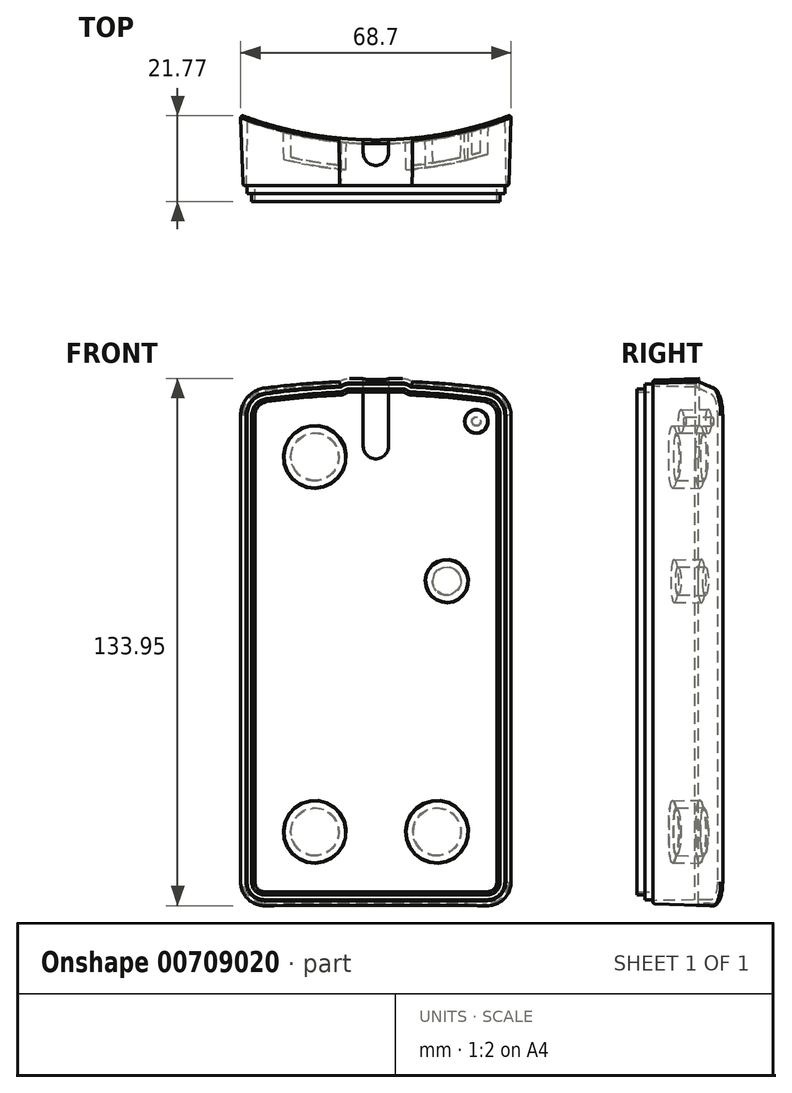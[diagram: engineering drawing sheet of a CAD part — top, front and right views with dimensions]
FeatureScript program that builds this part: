
annotation { "Feature Type Name" : "Feature", "Feature Type Description" : "" }
export const myFeature = defineFeature(function(context is Context, id is Id, definition is map)
    precondition{}
    {
        {
            var Q0;
            Q0=qCreatedBy(makeId("Front.planeOp"),FACE);
            var sketch = newSketch(context, id + "F0", { "sketchPlane" : qUnion([Q0])});
            skLineSegment(sketch, "E0.bottom", {"start": v(4.5, 0) * mm, "end": v(61, 0) * mm});
            skLineSegment(sketch, "E0.left", {"start": v(0, 4.5) * mm, "end": v(0, 123.05) * mm});
            skLineSegment(sketch, "E0.right", {"start": v(65.5, 4.5) * mm, "end": v(65.5, 123.05) * mm});
            skPoint(sketch, "E1.visualSharp", {"position": v(0, 0) * mm});
            skArc(sketch, "E1.filletArc", {"start": v(0, 4.5) * mm, "mid": v(1.32, 1.32) * mm, "end": v(4.5, 0) * mm});
            skPoint(sketch, "E2.visualSharp", {"position": v(65.5, 0) * mm});
            skArc(sketch, "E2.filletArc", {"start": v(61, 0) * mm, "mid": v(64.18, 1.32) * mm, "end": v(65.5, 4.5) * mm});
            skArc(sketch, "E3.filletArc", {"start": v(4.76, 128.5) * mm, "mid": v(1.36, 126.67) * mm, "end": v(0, 123.05) * mm});
            skPoint(sketch, "E4.visualSharp", {"position": v(65.5, 168.18) * mm});
            skArc(sketch, "E4.filletArc", {"start": v(65.5, 123.05) * mm, "mid": v(64.14, 126.67) * mm, "end": v(60.74, 128.5) * mm});
            skArc(sketch, "E5", {"start": v(60.74, 128.5) * mm, "mid": v(51.35, 129.57) * mm, "end": v(41.91, 130.2) * mm});
            skLineSegment(sketch, "E6", {"start": v(26, 131) * mm, "end": v(39.5, 131) * mm});
            skArc(sketch, "E7.trimOffspring", {"start": v(23.59, 130.2) * mm, "mid": v(14.15, 129.57) * mm, "end": v(4.76, 128.5) * mm});
            skLineSegment(sketch, "E8", {"start": v(32.75, 0) * mm, "end": v(32.75, 224.52) * mm, "construction": true});
            skArc(sketch, "E9", {"start": v(26, 131) * mm, "mid": v(25.02, 130.84) * mm, "end": v(24.13, 130.4) * mm});
            skPoint(sketch, "E10.visualSharp", {"position": v(23.91, 130.21) * mm});
            skArc(sketch, "E10.filletArc", {"start": v(23.59, 130.2) * mm, "mid": v(23.87, 130.26) * mm, "end": v(24.13, 130.4) * mm});
            skArc(sketch, "E11.MirrorCS", {"start": v(41.91, 130.2) * mm, "mid": v(41.63, 130.26) * mm, "end": v(41.37, 130.4) * mm});
            skArc(sketch, "E12.MirrorCS", {"start": v(39.5, 131) * mm, "mid": v(40.48, 130.84) * mm, "end": v(41.37, 130.4) * mm});
            skSolve(sketch);
        }
        {
            var Q0;
            Q0=qCreatedBy(makeId("Top.planeOp"),FACE);
            var sketch = newSketch(context, id + "F1", { "sketchPlane" : qUnion([Q0])});
            skArc(sketch, "E13", {"start": v(0, 0) * mm, "mid": v(32.75, -5.75) * mm, "end": v(65.5, 0) * mm});
            skLineSegment(sketch, "E14", {"start": v(0, 0) * mm, "end": v(65.5, 0) * mm});
            skLineSegment(sketch, "E15", {"start": v(0, 0) * mm, "end": v(94.5, 0) * mm, "construction": true});
            skLineSegment(sketch, "E16", {"start": v(94.5, 0) * mm, "end": v(32.75, 0) * mm, "construction": true});
            skLineSegment(sketch, "E17", {"start": v(32.75, 0) * mm, "end": v(32.75, -16.7) * mm, "construction": true});
            skSolve(sketch);
        }
        {
            var Q0;
            Q0=qSketchRegion(id+"F0",true);
            extrude(context, id + "F2", {"entities" : qUnion([Q0]), "depth" : 12.5 * mm, "offsetDistance" : 25 * mm});
        }
        {
            var Q0;
            Q0=qSketchRegion(id+"F1",true);
            extrude(context, id + "F3", {"entities" : qUnion([Q0]), "operationType" : NewBodyOperationType.REMOVE, "endBound" : BoundingType.THROUGH_ALL, "depth" : 25 * mm, "offsetDistance" : 25 * mm});
        }
        {
            var Q0;
            Q0=makeQuery(id+"F2.opExtrude","SWEPT_FACE",FACE,{"disambiguationData":[OSD([sQuery(id+"F0.wireOp",EDGE,"E0.bottom")])]});
            var sketch = newSketch(context, id + "F4", { "sketchPlane" : qUnion([Q0])});
            skLineSegment(sketch, "E18", {"start": v(0, 12.5) * mm, "end": v(0, 10.5) * mm});
            skLineSegment(sketch, "E19", {"start": v(0, 10.5) * mm, "end": v(1.1, 10.5) * mm});
            skLineSegment(sketch, "E20", {"start": v(1.1, 10.5) * mm, "end": v(1.1, 12.5) * mm});
            skLineSegment(sketch, "E21", {"start": v(1.1, 12.5) * mm, "end": v(0, 12.5) * mm});
            skSolve(sketch);
        }
        {
            var Q0;
            Q0=makeQuery(id+"F4.imprint","IMPRINT",FACE,{"disambiguationData":[TD([[makeQuery(id+"F4.imprint","IMPRINT",EDGE,{"derivedFrom":sQuery(id+"F4.wireOp",EDGE,"E18")}),1.0]])]});
            cPlane(context, id + "F5", {"entities" : qUnion([Q0]), "cplaneType" : CPlaneType.OFFSET, "offset" : 50 * mm, "oppositeDirection" : true, "width" : 150 * mm, "height" : 150 * mm});
        }
        {
            var Q0;
            Q0=makeQuery(id+"F2.opExtrude","CAP_FACE",FACE,{"disambiguationData":[OSD([sQuery(id+"F0.wireOp",EDGE,"E0.bottom"),sQuery(id+"F0.wireOp",EDGE,"E0.left"),sQuery(id+"F0.wireOp",EDGE,"E0.right"),sQuery(id+"F0.wireOp",EDGE,"E1.filletArc"),sQuery(id+"F0.wireOp",EDGE,"E2.filletArc"),sQuery(id+"F0.wireOp",EDGE,"E3.filletArc"),sQuery(id+"F0.wireOp",EDGE,"E4.filletArc"),sQuery(id+"F0.wireOp",EDGE,"E5"),sQuery(id+"F0.wireOp",EDGE,"E6"),sQuery(id+"F0.wireOp",EDGE,"4cuLOFSM-Cs9p-uLwk-Nxmp-eiNM5esqOte1"),sQuery(id+"F0.wireOp",EDGE,"qXNs2k06-4niP-ImqC-5Hru-JPzRlnRtqvzY"),sQuery(id+"F0.wireOp",EDGE,"592cab12-c6ad-4f12-8fa5-e9ea6a7a9ab5.filletArc"),sQuery(id+"F0.wireOp",EDGE,"E7.trimOffspring"),sQuery(id+"F0.wireOp",EDGE,"810a662d-7d86-4de4-b075-b749f1e53ed9.filletArc"),sQuery(id+"F0.wireOp",EDGE,"8d541c61-4af1-470d-ac14-312aa46fb37d.filletArc"),sQuery(id+"F0.wireOp",EDGE,"225b199f-dbc8-4900-9de2-33667acb90c7.filletArc")])],"isStart":false});
            shell(context, id + "F6", {"entities" : qUnion([Q0]), "thickness" : 2 * mm});
        }
        {
            var Q0;
            Q0=makeQuery(id+"F2.opExtrude","CAP_FACE",FACE,{"disambiguationData":[OSD([sQuery(id+"F0.wireOp",EDGE,"E0.bottom"),sQuery(id+"F0.wireOp",EDGE,"E0.left"),sQuery(id+"F0.wireOp",EDGE,"E0.right"),sQuery(id+"F0.wireOp",EDGE,"E1.filletArc"),sQuery(id+"F0.wireOp",EDGE,"E2.filletArc"),sQuery(id+"F0.wireOp",EDGE,"E3.filletArc"),sQuery(id+"F0.wireOp",EDGE,"E4.filletArc"),sQuery(id+"F0.wireOp",EDGE,"E5"),sQuery(id+"F0.wireOp",EDGE,"E6"),sQuery(id+"F0.wireOp",EDGE,"E7.trimOffspring"),sQuery(id+"F0.wireOp",EDGE,"E9"),sQuery(id+"F0.wireOp",EDGE,"E10.filletArc"),sQuery(id+"F0.wireOp",EDGE,"E11.MirrorCS"),sQuery(id+"F0.wireOp",EDGE,"E12.MirrorCS")])],"isStart":false});
            var sketch = newSketch(context, id + "F7", { "sketchPlane" : qUnion([Q0])});
            skLineSegment(sketch, "E22.0.0", {"start": v(39.5, 131) * mm, "end": v(26, 131) * mm});
            skArc(sketch, "E22.0.1", {"start": v(26, 131) * mm, "mid": v(25.02, 130.84) * mm, "end": v(24.13, 130.4) * mm});
            skArc(sketch, "E22.0.2", {"start": v(24.13, 130.4) * mm, "mid": v(23.87, 130.26) * mm, "end": v(23.59, 130.2) * mm});
            skArc(sketch, "E22.0.3", {"start": v(23.59, 130.2) * mm, "mid": v(14.15, 129.57) * mm, "end": v(4.76, 128.5) * mm});
            skArc(sketch, "E22.0.4", {"start": v(4.76, 128.5) * mm, "mid": v(1.36, 126.67) * mm, "end": v(0, 123.05) * mm});
            skLineSegment(sketch, "E22.0.5", {"start": v(0, 123.05) * mm, "end": v(0, 4.5) * mm});
            skArc(sketch, "E22.0.6", {"start": v(0, 4.5) * mm, "mid": v(1.32, 1.32) * mm, "end": v(4.5, 0) * mm});
            skLineSegment(sketch, "E22.0.7", {"start": v(4.5, 0) * mm, "end": v(61, 0) * mm});
            skArc(sketch, "E22.0.8", {"start": v(61, 0) * mm, "mid": v(64.18, 1.32) * mm, "end": v(65.5, 4.5) * mm});
            skLineSegment(sketch, "E22.0.9", {"start": v(65.5, 4.5) * mm, "end": v(65.5, 123.05) * mm});
            skArc(sketch, "E22.0.10", {"start": v(65.5, 123.05) * mm, "mid": v(64.14, 126.67) * mm, "end": v(60.74, 128.5) * mm});
            skArc(sketch, "E22.0.11", {"start": v(60.74, 128.5) * mm, "mid": v(51.35, 129.57) * mm, "end": v(41.91, 130.2) * mm});
            skArc(sketch, "E22.0.12", {"start": v(41.91, 130.2) * mm, "mid": v(41.63, 130.26) * mm, "end": v(41.37, 130.4) * mm});
            skArc(sketch, "E22.0.13", {"start": v(41.37, 130.4) * mm, "mid": v(40.48, 130.84) * mm, "end": v(39.5, 131) * mm});
            skArc(sketch, "E23.0", {"start": v(40.66, 129.42) * mm, "mid": v(40.1, 129.7) * mm, "end": v(39.5, 129.8) * mm});
            skArc(sketch, "E23.1", {"start": v(41.86, 129) * mm, "mid": v(41.23, 129.12) * mm, "end": v(40.66, 129.42) * mm});
            skArc(sketch, "E23.2", {"start": v(60.58, 127.31) * mm, "mid": v(51.24, 128.37) * mm, "end": v(41.86, 129) * mm});
            skArc(sketch, "E23.3", {"start": v(4.92, 127.31) * mm, "mid": v(2.26, 125.88) * mm, "end": v(1.2, 123.05) * mm});
            skArc(sketch, "E23.4", {"start": v(23.64, 129) * mm, "mid": v(14.26, 128.37) * mm, "end": v(4.92, 127.31) * mm});
            skArc(sketch, "E23.5", {"start": v(24.84, 129.42) * mm, "mid": v(24.27, 129.12) * mm, "end": v(23.64, 129) * mm});
            skArc(sketch, "E23.6", {"start": v(26, 129.8) * mm, "mid": v(25.4, 129.7) * mm, "end": v(24.84, 129.42) * mm});
            skLineSegment(sketch, "E23.7", {"start": v(1.2, 123.05) * mm, "end": v(1.2, 4.5) * mm});
            skArc(sketch, "E23.8", {"start": v(1.2, 4.5) * mm, "mid": v(2.17, 2.17) * mm, "end": v(4.5, 1.2) * mm});
            skLineSegment(sketch, "E23.9", {"start": v(4.5, 1.2) * mm, "end": v(61, 1.2) * mm});
            skLineSegment(sketch, "E23.10", {"start": v(39.5, 129.8) * mm, "end": v(26, 129.8) * mm});
            skArc(sketch, "E23.11", {"start": v(61, 1.2) * mm, "mid": v(63.33, 2.17) * mm, "end": v(64.3, 4.5) * mm});
            skLineSegment(sketch, "E23.12", {"start": v(64.3, 4.5) * mm, "end": v(64.3, 123.05) * mm});
            skArc(sketch, "E23.13", {"start": v(64.3, 123.05) * mm, "mid": v(63.24, 125.88) * mm, "end": v(60.58, 127.31) * mm});
            skSolve(sketch);
        }
        {
            var Q0;
            Q0=qSketchRegion(id+"F7",true);
            extrude(context, id + "F8", {"entities" : qUnion([Q0]), "operationType" : NewBodyOperationType.REMOVE, "oppositeDirection" : true, "depth" : 2 * mm, "offsetDistance" : 25 * mm});
        }
        {
            var Q0;
            Q0=makeQuery(id+"F6.opShell","OFFSET_EDGE",EDGE,{"disambiguationData":[OSD([sQuery(id+"F0.wireOp",EDGE,"E7.trimOffspring")])]});
            var Q1;
            Q1=makeQuery(id+"F8.boolean.opBoolean","COPY",EDGE,{"derivedFrom":makeQuery(id+"F8.opExtrude","CAP_EDGE",EDGE,{"disambiguationData":[OSD([sQuery(id+"F7.wireOp",EDGE,"E23.4")])],"isStart":true})});
            fillet(context, id + "F9", {"entities" : qUnion([Q0, Q1]), "radius" : .2 * mm, "tangentPropagation" : true, "allowEdgeOverflow" : false});
        }
        {
            var Q0;
            Q0=qCreatedBy(makeId("Front.planeOp"),FACE);
            var sketch = newSketch(context, id + "F10", { "sketchPlane" : qUnion([Q0])});
            skCircle(sketch, "E24", {"center": v(52.88, 68) * mm, "radius": 5.12 * mm});
            skArc(sketch, "E25", {"start": v(16.47, 64.05) * mm, "mid": v(12.44, 73) * mm, "end": v(9.49, 63.64) * mm});
            skArc(sketch, "E26", {"start": v(10.62, 44.32) * mm, "mid": v(14.94, 30.41) * mm, "end": v(17.6, 44.73) * mm});
            skLineSegment(sketch, "E27", {"start": v(12.75, 67.75) * mm, "end": v(14.5, 37.9) * mm, "construction": true});
            skLineSegment(sketch, "E28", {"start": v(16.47, 64.05) * mm, "end": v(17.6, 44.73) * mm});
            skLineSegment(sketch, "E29.MirrorCS", {"start": v(9.49, 63.64) * mm, "end": v(10.62, 44.32) * mm});
            skSolve(sketch);
        }
        {
            var Q0;
            Q0=qSketchRegion(id+"F10",true);
            extrude(context, id + "F11", {"entities" : qUnion([Q0]), "operationType" : NewBodyOperationType.REMOVE, "endBound" : BoundingType.THROUGH_ALL, "depth" : 25 * mm, "offsetDistance" : 25 * mm});
        }
        {
            var Q0;
            Q0=qCreatedBy(makeId("Front.planeOp"),FACE);
            var sketch = newSketch(context, id + "F12", { "sketchPlane" : qUnion([Q0])});
            skLineSegment(sketch, "E30", {"start": v(51.75, 114.46) * mm, "end": v(32.54, 67.75) * mm, "construction": true});
            skArc(sketch, "E31.0.startCap", {"start": v(49.2, 115.5) * mm, "mid": v(52.8, 117) * mm, "end": v(54.3, 113.41) * mm});
            skArc(sketch, "E31.0.endCap", {"start": v(35.09, 66.7) * mm, "mid": v(31.5, 65.2) * mm, "end": v(30, 68.8) * mm});
            skLineSegment(sketch, "E31.0.left", {"start": v(54.3, 113.41) * mm, "end": v(35.09, 66.7) * mm});
            skLineSegment(sketch, "E31.0.right", {"start": v(49.2, 115.5) * mm, "end": v(30, 68.8) * mm});
            skLineSegment(sketch, "E32.0", {"start": v(48.28, 115.89) * mm, "end": v(29.08, 69.18) * mm});
            skArc(sketch, "E32.1", {"start": v(48.28, 115.89) * mm, "mid": v(53.18, 117.93) * mm, "end": v(55.22, 113.03) * mm});
            skLineSegment(sketch, "E32.2", {"start": v(55.22, 113.03) * mm, "end": v(36.01, 66.32) * mm});
            skArc(sketch, "E32.3", {"start": v(36.01, 66.32) * mm, "mid": v(31.12, 64.28) * mm, "end": v(29.08, 69.18) * mm});
            skSolve(sketch);
        }
        {
            var Q0;
            {var subQ0=sQuery(id+"F1.wireOp",EDGE,"E14");var subQ1=sQuery(id+"F1.wireOp",EDGE,"E13");Q0=makeQuery(id+"F3.boolean.opBoolean","MERGE",EDGE,{"derivedFrom":[makeQuery(id+"F2.opExtrude","CAP_EDGE",EDGE,{"disambiguationData":[OSD([sQuery(id+"F0.wireOp",EDGE,"E0.left")])],"isStart":true}),makeQuery(id+"F3.opExtrude","SWEPT_EDGE",EDGE,{"disambiguationData":[OSD([subQ1,subQ0]),TDD([makeQuery(id+"F1.imprint","INTERSECT",VERTEX,{"disambiguationData":[OD(0.0)],"derivedFrom":[subQ1,subQ0]})])]})]});}
            fillet(context, id + "F13", {"entities" : qUnion([Q0]), "radius" : .5 * mm, "tangentPropagation" : true, "allowEdgeOverflow" : false});
        }
        {
            var Q0;
            Q0=qSketchRegion(id+"F12",true);
            var Q1;
            Q1=makeQuery(id+"F3.boolean.opBoolean","COPY",FACE,{"derivedFrom":makeQuery(id+"F3.opExtrude","SWEPT_FACE",FACE,{"disambiguationData":[OSD([sQuery(id+"F1.wireOp",EDGE,"E13")])]})});
            var Q2;
            Q2=makeQuery(id+"F2.opExtrude","SWEPT_BODY",BODY,{"disambiguationData":[OSD([sQuery(id+"F0.wireOp",EDGE,"E0.bottom"),sQuery(id+"F0.wireOp",EDGE,"E0.left"),sQuery(id+"F0.wireOp",EDGE,"E0.right"),sQuery(id+"F0.wireOp",EDGE,"E1.filletArc"),sQuery(id+"F0.wireOp",EDGE,"E2.filletArc"),sQuery(id+"F0.wireOp",EDGE,"E3.filletArc"),sQuery(id+"F0.wireOp",EDGE,"E4.filletArc"),sQuery(id+"F0.wireOp",EDGE,"E5"),sQuery(id+"F0.wireOp",EDGE,"E6"),sQuery(id+"F0.wireOp",EDGE,"E7.trimOffspring"),sQuery(id+"F0.wireOp",EDGE,"E9"),sQuery(id+"F0.wireOp",EDGE,"E10.filletArc"),sQuery(id+"F0.wireOp",EDGE,"E11.MirrorCS"),sQuery(id+"F0.wireOp",EDGE,"E12.MirrorCS")])]});
            var Q3;
            Q3=makeQuery(id+"F3.boolean.opBoolean","COPY",FACE,{"derivedFrom":makeQuery(id+"F3.opExtrude","SWEPT_FACE",FACE,{"disambiguationData":[OSD([sQuery(id+"F1.wireOp",EDGE,"E13")])]})});
            extrude(context, id + "F14", {"entities" : qUnion([Q0]), "operationType" : NewBodyOperationType.ADD, "endBound" : BoundingType.UP_TO_SURFACE, "depth" : 25 * mm, "endBoundEntityFace" : qUnion([Q1]), "endBoundEntityBody" : qUnion([Q2]), "offsetDistance" : 1 * mm, "offsetOppositeDirection" : true, "hasSecondDirection" : true, "secondDirectionBound" : BoundingType.UP_TO_SURFACE, "secondDirectionOppositeDirection" : false, "secondDirectionDepth" : 1 * mm, "secondDirectionBoundEntityFace" : qUnion([Q3]), "hasSecondDirectionOffset" : true, "secondDirectionOffsetDistance" : .5 * mm});
        }
        {
            var Q0;
            Q0=makeQuery(id+"F14.opExtrude","CAP_EDGE",EDGE,{"disambiguationData":[OSD([sQuery(id+"F12.wireOp",EDGE,"E31.0.left")])],"isStart":true});
            var Q1;
            Q1=makeQuery(id+"F14.opExtrude","CAP_EDGE",EDGE,{"disambiguationData":[OSD([sQuery(id+"F12.wireOp",EDGE,"E32.2")])],"isStart":true});
            fillet(context, id + "F15", {"entities" : qUnion([Q0, Q1]), "radius" : .5 * mm, "tangentPropagation" : true, "allowEdgeOverflow" : false});
        }
        {
            var Q0;
            Q0=qCreatedBy(makeId("Front.planeOp"),FACE);
            var sketch = newSketch(context, id + "F16", { "sketchPlane" : qUnion([Q0])});
            skCircle(sketch, "E33", {"center": v(51.75, 114.46) * mm, "radius": 0.75 * mm});
            skLineSegment(sketch, "E34.0", {"start": v(51.75, 114.46) * mm, "end": v(32.54, 67.75) * mm, "construction": true});
            skSolve(sketch);
        }
        {
            var Q0;
            Q0=makeQuery(id+"F16.imprint","IMPRINT",FACE,{"disambiguationData":[TD([[makeQuery(id+"F16.imprint","IMPRINT",EDGE,{"derivedFrom":sQuery(id+"F16.wireOp",EDGE,"E33")}),1.0]])]});
            var Q1;
            Q1=qConstructionFilter(qBodyType(qCreatedBy(id+"F16",EDGE),BodyType.WIRE),ConstructionObject.NO);
            extrude(context, id + "F17", {"entities" : qUnion([Q0]), "operationType" : NewBodyOperationType.REMOVE, "surfaceEntities" : qUnion([Q1]), "endBound" : BoundingType.THROUGH_ALL, "depth" : 25 * mm, "offsetDistance" : 25 * mm});
        }
        {
            var Q0;
            Q0=qCreatedBy(makeId("Top.planeOp"),FACE);
            var sketch = newSketch(context, id + "F18", { "sketchPlane" : qUnion([Q0])});
            skLineSegment(sketch, "E35.0", {"start": v(-0.5, -7.5) * mm, "end": v(-0.5, 1.21) * mm});
            skLineSegment(sketch, "E35.1", {"start": v(66, -7.57) * mm, "end": v(66, 1.14) * mm});
            skLineSegment(sketch, "E36", {"start": v(32.75, -4) * mm, "end": v(32.75, 0.99) * mm, "construction": true});
            skPoint(sketch, "E36.startSnap0", {"position": v(32.75, -4) * mm});
            skArc(sketch, "E37.0", {"start": v(66, 1.14) * mm, "mid": v(32.75, -4.75) * mm, "end": v(-0.5, 1.21) * mm});
            skSolve(sketch);
        }
        {
            var Q0;
            Q0=makeQuery(id+"F8.boolean.opBoolean","COPY",FACE,{"derivedFrom":makeQuery(id+"F8.opExtrude","CAP_FACE",FACE,{"disambiguationData":[OSD([sQuery(id+"F7.wireOp",EDGE,"E22.0.0"),sQuery(id+"F7.wireOp",EDGE,"E22.0.1"),sQuery(id+"F7.wireOp",EDGE,"E22.0.2"),sQuery(id+"F7.wireOp",EDGE,"E22.0.3"),sQuery(id+"F7.wireOp",EDGE,"E22.0.4"),sQuery(id+"F7.wireOp",EDGE,"E22.0.5"),sQuery(id+"F7.wireOp",EDGE,"E22.0.6"),sQuery(id+"F7.wireOp",EDGE,"E22.0.7"),sQuery(id+"F7.wireOp",EDGE,"E22.0.8"),sQuery(id+"F7.wireOp",EDGE,"E22.0.9"),sQuery(id+"F7.wireOp",EDGE,"E22.0.10"),sQuery(id+"F7.wireOp",EDGE,"E22.0.11"),sQuery(id+"F7.wireOp",EDGE,"E22.0.12"),sQuery(id+"F7.wireOp",EDGE,"E22.0.13"),sQuery(id+"F7.wireOp",EDGE,"E23.0"),sQuery(id+"F7.wireOp",EDGE,"E23.1"),sQuery(id+"F7.wireOp",EDGE,"E23.2"),sQuery(id+"F7.wireOp",EDGE,"E23.3"),sQuery(id+"F7.wireOp",EDGE,"E23.4"),sQuery(id+"F7.wireOp",EDGE,"E23.5"),sQuery(id+"F7.wireOp",EDGE,"E23.6"),sQuery(id+"F7.wireOp",EDGE,"E23.7"),sQuery(id+"F7.wireOp",EDGE,"E23.8"),sQuery(id+"F7.wireOp",EDGE,"E23.9"),sQuery(id+"F7.wireOp",EDGE,"E23.10"),sQuery(id+"F7.wireOp",EDGE,"E23.11"),sQuery(id+"F7.wireOp",EDGE,"E23.12"),sQuery(id+"F7.wireOp",EDGE,"E23.13")])],"isStart":false})});
            cPlane(context, id + "F19", {"entities" : qUnion([Q0]), "cplaneType" : CPlaneType.OFFSET, "offset" : 2 * mm, "oppositeDirection" : true, "width" : 150 * mm, "height" : 150 * mm});
        }
        {
            var Q0;
            Q0=qCreatedBy(id+"F19.planeOp",FACE);
            var sketch = newSketch(context, id + "F20", { "sketchPlane" : qUnion([Q0])});
            skLineSegment(sketch, "E38.0.0", {"start": v(39.5, 131) * mm, "end": v(26, 131) * mm});
            skArc(sketch, "E38.0.1", {"start": v(26, 131) * mm, "mid": v(25.02, 130.84) * mm, "end": v(24.13, 130.4) * mm});
            skArc(sketch, "E38.0.2", {"start": v(24.13, 130.4) * mm, "mid": v(23.87, 130.26) * mm, "end": v(23.59, 130.2) * mm});
            skArc(sketch, "E38.0.3", {"start": v(23.59, 130.2) * mm, "mid": v(14.15, 129.57) * mm, "end": v(4.76, 128.5) * mm});
            skArc(sketch, "E38.0.4", {"start": v(4.76, 128.5) * mm, "mid": v(1.36, 126.67) * mm, "end": v(0, 123.05) * mm});
            skLineSegment(sketch, "E38.0.5", {"start": v(0, 123.05) * mm, "end": v(0, 4.5) * mm});
            skArc(sketch, "E38.0.6", {"start": v(0, 4.5) * mm, "mid": v(1.32, 1.32) * mm, "end": v(4.5, 0) * mm});
            skLineSegment(sketch, "E38.0.7", {"start": v(4.5, 0) * mm, "end": v(61, 0) * mm});
            skArc(sketch, "E38.0.8", {"start": v(61, 0) * mm, "mid": v(64.18, 1.32) * mm, "end": v(65.5, 4.5) * mm});
            skLineSegment(sketch, "E38.0.9", {"start": v(65.5, 4.5) * mm, "end": v(65.5, 123.05) * mm});
            skArc(sketch, "E38.0.10", {"start": v(65.5, 123.05) * mm, "mid": v(64.14, 126.67) * mm, "end": v(60.74, 128.5) * mm});
            skArc(sketch, "E38.0.11", {"start": v(60.74, 128.5) * mm, "mid": v(51.35, 129.57) * mm, "end": v(41.91, 130.2) * mm});
            skArc(sketch, "E38.0.12", {"start": v(41.91, 130.2) * mm, "mid": v(41.63, 130.26) * mm, "end": v(41.37, 130.4) * mm});
            skArc(sketch, "E38.0.13", {"start": v(41.37, 130.4) * mm, "mid": v(40.48, 130.84) * mm, "end": v(39.5, 131) * mm});
            skLineSegment(sketch, "E39.0", {"start": v(4.5, -1) * mm, "end": v(61, -1) * mm});
            skArc(sketch, "E39.1", {"start": v(41.96, 131.2) * mm, "mid": v(40.8, 131.8) * mm, "end": v(39.5, 132) * mm});
            skArc(sketch, "E39.2", {"start": v(60.88, 129.5) * mm, "mid": v(51.44, 130.56) * mm, "end": v(41.96, 131.2) * mm});
            skArc(sketch, "E39.3", {"start": v(66.5, 123.05) * mm, "mid": v(64.9, 127.32) * mm, "end": v(60.88, 129.5) * mm});
            skLineSegment(sketch, "E39.4", {"start": v(66.5, 4.5) * mm, "end": v(66.5, 123.05) * mm});
            skLineSegment(sketch, "E39.5", {"start": v(39.5, 132) * mm, "end": v(26, 132) * mm});
            skArc(sketch, "E39.6", {"start": v(61, -1) * mm, "mid": v(64.89, 0.61) * mm, "end": v(66.5, 4.5) * mm});
            skArc(sketch, "E39.7", {"start": v(26, 132) * mm, "mid": v(24.7, 131.8) * mm, "end": v(23.54, 131.2) * mm});
            skArc(sketch, "E39.8", {"start": v(23.54, 131.2) * mm, "mid": v(14.06, 130.56) * mm, "end": v(4.62, 129.5) * mm});
            skArc(sketch, "E39.9", {"start": v(4.62, 129.5) * mm, "mid": v(0.6, 127.32) * mm, "end": v(-1, 123.05) * mm});
            skLineSegment(sketch, "E39.10", {"start": v(-1, 123.05) * mm, "end": v(-1, 4.5) * mm});
            skArc(sketch, "E39.11", {"start": v(-1, 4.5) * mm, "mid": v(0.61, 0.61) * mm, "end": v(4.5, -1) * mm});
            skArc(sketch, "E40.0", {"start": v(4.72, 128.75) * mm, "mid": v(1.17, 126.83) * mm, "end": v(-0.25, 123.05) * mm});
            skLineSegment(sketch, "E40.1", {"start": v(65.75, 4.5) * mm, "end": v(65.75, 123.05) * mm});
            skArc(sketch, "E40.2", {"start": v(61, -0.25) * mm, "mid": v(64.36, 1.14) * mm, "end": v(65.75, 4.5) * mm});
            skLineSegment(sketch, "E40.3", {"start": v(4.5, -0.25) * mm, "end": v(61, -0.25) * mm});
            skArc(sketch, "E40.4", {"start": v(-0.25, 4.5) * mm, "mid": v(1.14, 1.14) * mm, "end": v(4.5, -0.25) * mm});
            skArc(sketch, "E40.5", {"start": v(65.75, 123.05) * mm, "mid": v(64.33, 126.83) * mm, "end": v(60.78, 128.75) * mm});
            skLineSegment(sketch, "E40.6", {"start": v(-0.25, 123.05) * mm, "end": v(-0.25, 4.5) * mm});
            skArc(sketch, "E40.7", {"start": v(60.78, 128.75) * mm, "mid": v(51.25, 129.82) * mm, "end": v(41.68, 130.46) * mm});
            skArc(sketch, "E40.8", {"start": v(41.68, 130.46) * mm, "mid": v(40.66, 131.05) * mm, "end": v(39.5, 131.25) * mm});
            skLineSegment(sketch, "E40.9", {"start": v(39.5, 131.25) * mm, "end": v(26, 131.25) * mm});
            skArc(sketch, "E40.10", {"start": v(26, 131.25) * mm, "mid": v(24.84, 131.05) * mm, "end": v(23.82, 130.46) * mm});
            skArc(sketch, "E40.11", {"start": v(23.82, 130.46) * mm, "mid": v(14.25, 129.82) * mm, "end": v(4.72, 128.75) * mm});
            skSolve(sketch);
        }
        {
            var Q0;
            Q0=makeQuery(id+"F20.imprint","IMPRINT",FACE,{"disambiguationData":[TD([[makeQuery(id+"F20.imprint","IMPRINT",EDGE,{"derivedFrom":sQuery(id+"F20.wireOp",EDGE,"E38.0.0")}),-1.0]])]});
            var Q1;
            Q1=makeQuery(id+"F20.imprint","IMPRINT",FACE,{"disambiguationData":[TD([[makeQuery(id+"F20.imprint","IMPRINT",EDGE,{"derivedFrom":sQuery(id+"F20.wireOp",EDGE,"E38.0.0")}),1.0]])]});
            var Q2;
            Q2=makeQuery(id+"F20.imprint","IMPRINT",FACE,{"disambiguationData":[TD([[makeQuery(id+"F20.imprint","IMPRINT",EDGE,{"derivedFrom":sQuery(id+"F20.wireOp",EDGE,"E39.0")}),1.0]])]});
            extrude(context, id + "F21", {"entities" : qUnion([Q0, Q1, Q2]), "oppositeDirection" : true, "depth" : 18 * mm, "offsetDistance" : 25 * mm, "hasDraft" : true, "draftAngle" : 2 * degree});
        }
        {
            var Q0;
            Q0=qCreatedBy(makeId("Top.planeOp"),FACE);
            var sketch = newSketch(context, id + "F22", { "sketchPlane" : qUnion([Q0])});
            skLineSegment(sketch, "E41.0.0", {"start": v(61, -8.5) * mm, "end": v(4.5, -8.5) * mm, "construction": true});
            skLineSegment(sketch, "E41.0.1", {"start": v(4.5, 9.5) * mm, "end": v(4.5, -8.5) * mm, "construction": true});
            skLineSegment(sketch, "E41.0.2", {"start": v(4.5, 9.5) * mm, "end": v(61, 9.5) * mm, "construction": true});
            skLineSegment(sketch, "E41.0.3", {"start": v(61, 9.5) * mm, "end": v(61, -8.5) * mm, "construction": true});
            skLineSegment(sketch, "E41.1.0", {"start": v(66.5, -8.5) * mm, "end": v(61, -8.5) * mm, "construction": true});
            skLineSegment(sketch, "E41.1.1", {"start": v(61, 9.5) * mm, "end": v(61, -8.5) * mm, "construction": true});
            skLineSegment(sketch, "E41.1.2", {"start": v(61, 9.5) * mm, "end": v(67.13, 9.5) * mm, "construction": true});
            skLineSegment(sketch, "E41.1.3", {"start": v(67.13, 9.5) * mm, "end": v(66.5, -8.5) * mm, "construction": true});
            skLineSegment(sketch, "E41.2.0", {"start": v(4.5, -8.5) * mm, "end": v(-1, -8.5) * mm, "construction": true});
            skLineSegment(sketch, "E41.2.1", {"start": v(-1.63, 9.5) * mm, "end": v(-1, -8.5) * mm, "construction": true});
            skLineSegment(sketch, "E41.2.2", {"start": v(-1.63, 9.5) * mm, "end": v(4.5, 9.5) * mm, "construction": true});
            skLineSegment(sketch, "E41.2.3", {"start": v(4.5, 9.5) * mm, "end": v(4.5, -8.5) * mm, "construction": true});
            skArc(sketch, "E42", {"start": v(-1.63, 9.5) * mm, "mid": v(32.75, 3.14) * mm, "end": v(67.13, 9.5) * mm});
            skLineSegment(sketch, "E43", {"start": v(-1.63, 9.5) * mm, "end": v(67.13, 9.5) * mm});
            skSolve(sketch);
        }
        {
            var Q0;
            Q0=makeQuery(id+"F22.imprint","IMPRINT",FACE,{"disambiguationData":[TD([[makeQuery(id+"F22.imprint","IMPRINT",EDGE,{"derivedFrom":sQuery(id+"F22.wireOp",EDGE,"E42")}),1.0]])]});
            extrude(context, id + "F23", {"entities" : qUnion([Q0]), "operationType" : NewBodyOperationType.REMOVE, "endBound" : BoundingType.THROUGH_ALL, "oppositeDirection" : true, "depth" : 25 * mm, "offsetDistance" : 25 * mm, "hasSecondDirection" : true, "secondDirectionBound" : BoundingType.THROUGH_ALL, "secondDirectionOppositeDirection" : false, "secondDirectionDepth" : 25 * mm});
        }
        {
            var Q0;
            Q0=qCreatedBy(makeId("Top.planeOp"),FACE);
            cPlane(context, id + "F24", {"entities" : qUnion([Q0]), "cplaneType" : CPlaneType.OFFSET, "offset" : 6.5 * mm, "oppositeDirection" : true, "width" : 150 * mm, "height" : 150 * mm});
        }
        {
            var Q0;
            Q0=sQuery(id+"F18.wireOp",EDGE,"E37.0");
            extrude(context, id + "F25", {"bodyType" : ToolBodyType.SURFACE, "surfaceEntities" : qUnion([Q0]), "oppositeDirection" : true, "depth" : 5 * mm, "offsetDistance" : 25 * mm, "hasSecondDirection" : true, "secondDirectionOppositeDirection" : false, "secondDirectionDepth" : 150 * mm});
        }
        {
            var Q0;
            Q0=qCreatedBy(id+"F24.planeOp",FACE);
            var sketch = newSketch(context, id + "F26", { "sketchPlane" : qUnion([Q0])});
            skArc(sketch, "E44.0", {"start": v(-0.75, 1.9) * mm, "mid": v(32.75, -4.13) * mm, "end": v(66.25, 1.9) * mm});
            skLineSegment(sketch, "E45.0.0", {"start": v(39.5, -10.5) * mm, "end": v(39.5, -6.01) * mm, "construction": true});
            skArc(sketch, "E45.0.1", {"start": v(39.5, -6.01) * mm, "mid": v(32.75, -6.25) * mm, "end": v(26, -6.01) * mm, "construction": true});
            skLineSegment(sketch, "E45.0.2", {"start": v(26, -6.01) * mm, "end": v(26, -10.5) * mm, "construction": true});
            skLineSegment(sketch, "E45.0.3", {"start": v(26, -10.5) * mm, "end": v(39.5, -10.5) * mm, "construction": true});
            skLineSegment(sketch, "E46", {"start": v(32.75, -10.5) * mm, "end": v(32.75, 21.11) * mm, "construction": true});
            skPoint(sketch, "E46.endSnap0", {"position": v(32.75, -6.25) * mm});
            skSolve(sketch);
        }
        {
            var Q0;
            Q0=sQuery(id+"F26.wireOp",EDGE,"E44.0");
            extrude(context, id + "F27", {"bodyType" : ToolBodyType.SURFACE, "surfaceEntities" : qUnion([Q0]), "depth" : 147.2 * mm, "offsetDistance" : 25 * mm});
        }
        {
            var Q0;
            Q0=qCreatedBy(makeId("Front.planeOp"),FACE);
            cPlane(context, id + "F28", {"entities" : qUnion([Q0]), "cplaneType" : CPlaneType.OFFSET, "offset" : 10 * mm, "oppositeDirection" : true, "width" : 150 * mm, "height" : 150 * mm});
        }
        {
            var Q0;
            Q0=sQuery(id+"F22.wireOp",EDGE,"E42");
            extrude(context, id + "F29", {"bodyType" : ToolBodyType.SURFACE, "surfaceEntities" : qUnion([Q0]), "oppositeDirection" : true, "depth" : 10 * mm, "offsetDistance" : 25 * mm, "hasSecondDirection" : true, "secondDirectionOppositeDirection" : false, "secondDirectionDepth" : 141.6 * mm});
        }
        {
            var Q0;
            Q0=makeQuery(id+"F29.opExtrude","SWEPT_BODY",BODY,{"disambiguationData":[OSD([sQuery(id+"F22.wireOp",EDGE,"E42")])]});
            transform(context, id + "F30", {"entities" : qUnion([Q0]), "transformType" : TransformType.TRANSLATION_3D, "dx" : 0 * mm, "dy" : -1 * mm, "dz" : 0 * mm, "makeCopy" : false});
        }
        {
            var Q0;
            Q0=qCreatedBy(makeId("Top.planeOp"),FACE);
            cPlane(context, id + "F31", {"entities" : qUnion([Q0]), "cplaneType" : CPlaneType.OFFSET, "offset" : 140.2 * mm, "width" : 150 * mm, "height" : 150 * mm});
        }
        {
            var Q0;
            Q0=qCreatedBy(id+"F31.planeOp",FACE);
            var sketch = newSketch(context, id + "F32", { "sketchPlane" : qUnion([Q0])});
            skLineSegment(sketch, "E47.0.0", {"start": v(26, 3.38) * mm, "end": v(26, -6.5) * mm, "construction": true});
            skLineSegment(sketch, "E47.0.1", {"start": v(26, -6.5) * mm, "end": v(39.5, -6.5) * mm, "construction": true});
            skLineSegment(sketch, "E47.0.2", {"start": v(39.5, 3.38) * mm, "end": v(39.5, -6.5) * mm, "construction": true});
            skArc(sketch, "E47.0.3", {"start": v(36, 3.2) * mm, "mid": v(32.75, 3.14) * mm, "end": v(29.5, 3.2) * mm});
            skLineSegment(sketch, "E48", {"start": v(32.75, -6.5) * mm, "end": v(32.75, 3.14) * mm, "construction": true});
            skLineSegment(sketch, "E49", {"start": v(29.5, 3.2) * mm, "end": v(29.5, -0.1) * mm});
            skLineSegment(sketch, "E50.MirrorCS", {"start": v(36, 3.2) * mm, "end": v(36, -0.1) * mm});
            skArc(sketch, "E51", {"start": v(29.5, -0.1) * mm, "mid": v(32.75, -3.36) * mm, "end": v(36, -0.1) * mm});
            skSolve(sketch);
        }
        {
            var Q0;
            Q0=qSketchRegion(id+"F32",true);
            var Q1;
            Q1=makeQuery(id+"FxRnPsP5aDpV4hF_4.boolean.opBoolean","COPY",FACE,{"derivedFrom":makeQuery(id+"FxRnPsP5aDpV4hF_4.opExtrude","SWEPT_FACE",FACE,{"disambiguationData":[OSD([sQuery(id+"FboPe016KZlA5BW_4.wireOp",EDGE,"JrRxvUNI-9erT-SvnR-dZue-gbEGpQV73Hoo")])]})});
            extrude(context, id + "F33", {"entities" : qUnion([Q0]), "operationType" : NewBodyOperationType.REMOVE, "oppositeDirection" : true, "depth" : 25 * mm, "endBoundEntityFace" : qUnion([Q1]), "hasOffset" : true, "offsetDistance" : 5 * mm, "offsetOppositeDirection" : true});
        }
        {
            var Q0;
            Q0=makeQuery(id+"F21.opExtrude","CAP_EDGE",EDGE,{"disambiguationData":[OSD([sQuery(id+"F20.wireOp",EDGE,"E39.2")])],"isStart":true});
            var Q1;
            Q1=makeQuery(id+"F21.opExtrude","CAP_EDGE",EDGE,{"disambiguationData":[OSD([sQuery(id+"F20.wireOp",EDGE,"E39.1")])],"isStart":true});
            fillet(context, id + "F34", {"entities" : qUnion([Q0, Q1]), "radius" : .5 * mm, "tangentPropagation" : true, "allowEdgeOverflow" : false});
        }
        {
            var Q0;
            Q0=qCreatedBy(makeId("Front.planeOp"),FACE);
            var sketch = newSketch(context, id + "F35", { "sketchPlane" : qUnion([Q0])});
            skArc(sketch, "E52.0", {"start": v(36, 115.24) * mm, "mid": v(32.75, 115.26) * mm, "end": v(29.5, 115.24) * mm});
            skArc(sketch, "E53", {"start": v(29.5, 115.24) * mm, "mid": v(32.75, 112.01) * mm, "end": v(36, 115.24) * mm});
            skSolve(sketch);
        }
        {
            var Q0;
            Q0=makeQuery(id+"F35.imprint","IMPRINT",FACE,{"disambiguationData":[TD([[makeQuery(id+"F35.imprint","IMPRINT",EDGE,{"derivedFrom":sQuery(id+"F35.wireOp",EDGE,"E52.0")}),1.0]])]});
            extrude(context, id + "F36", {"entities" : qUnion([Q0]), "operationType" : NewBodyOperationType.REMOVE, "endBound" : BoundingType.THROUGH_ALL, "oppositeDirection" : true, "depth" : 25 * mm, "offsetDistance" : 25 * mm});
        }
        {
            var Q0;
            Q0=makeQuery(id+"F20.imprint","IMPRINT",FACE,{"disambiguationData":[TD([[makeQuery(id+"F20.imprint","IMPRINT",EDGE,{"derivedFrom":sQuery(id+"F20.wireOp",EDGE,"E38.0.0")}),-1.0]])]});
            var Q1;
            Q1=makeQuery(id+"F20.imprint","IMPRINT",FACE,{"disambiguationData":[TD([[makeQuery(id+"F20.imprint","IMPRINT",EDGE,{"derivedFrom":sQuery(id+"F20.wireOp",EDGE,"E38.0.0")}),1.0]])]});
            var Q2;
            Q2=makeQuery(id+"F29.opExtrude","SWEPT_FACE",FACE,{"disambiguationData":[OSD([sQuery(id+"F22.wireOp",EDGE,"E42")])]});
            extrude(context, id + "F37", {"entities" : qUnion([Q0, Q1]), "operationType" : NewBodyOperationType.REMOVE, "endBound" : BoundingType.UP_TO_SURFACE, "oppositeDirection" : true, "depth" : 25 * mm, "endBoundEntityFace" : qUnion([Q2]), "offsetDistance" : 25 * mm, "hasDraft" : true, "draftAngle" : 1 * degree, "draftPullDirection" : true});
        }
        {
            var Q0;
            Q0=qCreatedBy(makeId("Front.planeOp"),FACE);
            cPlane(context, id + "F38", {"entities" : qUnion([Q0]), "cplaneType" : CPlaneType.OFFSET, "offset" : 25 * mm, "width" : 150 * mm, "height" : 150 * mm});
        }
        {
            var Q0;
            Q0=qCreatedBy(id+"F38.planeOp",FACE);
            var sketch = newSketch(context, id + "F39", { "sketchPlane" : qUnion([Q0])});
            skCircle(sketch, "E54", {"center": v(48.25, 17.25) * mm, "radius": 7.5 * mm});
            skLineSegment(sketch, "E55.0", {"start": v(4.5, -0.52) * mm, "end": v(61, -0.52) * mm, "construction": true});
            skLineSegment(sketch, "E56", {"start": v(32.75, -0.52) * mm, "end": v(32.75, 50.45) * mm, "construction": true});
            skCircle(sketch, "E57.MirrorC", {"center": v(17.25, 17.25) * mm, "radius": 7.5 * mm});
            skCircle(sketch, "E58.MirrorC", {"center": v(17.25, 112.52) * mm, "radius": 7.5 * mm});
            skCircle(sketch, "E59", {"center": v(50.75, 80.95) * mm, "radius": 5 * mm});
            skCircle(sketch, "E60", {"center": v(58.25, 121.52) * mm, "radius": 2.5 * mm});
            skSolve(sketch);
        }
        {
            var Q0;
            Q0 = qSketchRegion(id + "F39", true);
            var Q1;
            Q1=makeQuery(id+"F21.opExtrude","SWEPT_BODY",BODY,{"disambiguationData":[OSD([sQuery(id+"F20.wireOp",EDGE,"E39.0"),sQuery(id+"F20.wireOp",EDGE,"E39.1"),sQuery(id+"F20.wireOp",EDGE,"E39.2"),sQuery(id+"F20.wireOp",EDGE,"E39.3"),sQuery(id+"F20.wireOp",EDGE,"E39.4"),sQuery(id+"F20.wireOp",EDGE,"E39.5"),sQuery(id+"F20.wireOp",EDGE,"E39.6"),sQuery(id+"F20.wireOp",EDGE,"E39.7"),sQuery(id+"F20.wireOp",EDGE,"E39.8"),sQuery(id+"F20.wireOp",EDGE,"E39.9"),sQuery(id+"F20.wireOp",EDGE,"E39.10"),sQuery(id+"F20.wireOp",EDGE,"E39.11")])]});
            var Q2;
            Q2=makeQuery(id+"F25.opExtrude","SWEPT_FACE",FACE,{"disambiguationData":[OSD([sQuery(id+"F18.wireOp",EDGE,"E37.0")])]});
            extrude(context, id + "F40", {"entities" : qUnion([Q0]), "operationType" : NewBodyOperationType.ADD, "endBound" : BoundingType.UP_TO_BODY, "oppositeDirection" : true, "depth" : 25 * mm, "endBoundEntityBody" : qUnion([Q1]), "offsetDistance" : 25 * mm, "hasDraft" : true, "draftAngle" : 1 * degree, "hasSecondDirection" : true, "secondDirectionBound" : BoundingType.UP_TO_SURFACE, "secondDirectionOppositeDirection" : true, "secondDirectionDepth" : 25 * mm, "secondDirectionBoundEntityFace" : qUnion([Q2])});
        }
        {
            var Q0;
            Q0=qCreatedBy(makeId("Front.planeOp"),FACE);
            cPlane(context, id + "F41", {"entities" : qUnion([Q0]), "cplaneType" : CPlaneType.OFFSET, "offset" : 25 * mm, "oppositeDirection" : true, "width" : 150 * mm, "height" : 150 * mm});
        }
        {
            var Q0;
            Q0=qCreatedBy(id+"F41.planeOp",FACE);
            var sketch = newSketch(context, id + "F42", { "sketchPlane" : qUnion([Q0])});
            skCircle(sketch, "E61.0", {"center": v(17.25, 112.52) * mm, "radius": 6.5 * mm});
            skCircle(sketch, "E61.1", {"center": v(58.25, 121.52) * mm, "radius": 1.5 * mm});
            skCircle(sketch, "E61.2", {"center": v(50.75, 80.95) * mm, "radius": 4 * mm});
            skCircle(sketch, "E61.3", {"center": v(48.25, 17.25) * mm, "radius": 6.5 * mm});
            skLineSegment(sketch, "E61.4", {"start": v(32.75, -0.52) * mm, "end": v(32.75, 50.45) * mm, "construction": true});
            skCircle(sketch, "E61.5", {"center": v(17.25, 17.25) * mm, "radius": 6.5 * mm});
            skLineSegment(sketch, "E61.6", {"start": v(4.5, -0.52) * mm, "end": v(61, -0.52) * mm, "construction": true});
            skSolve(sketch);
        }
        {
            var Q0;
            Q0 = qSketchRegion(id + "F42", true);
            var Q1;
            Q1=makeQuery(id+"F40.opExtrude","CAP_FACE",FACE,{"disambiguationData":[OSD([sQuery(id+"F39.wireOp",EDGE,"E58.MirrorC")]),topologyDisambiguationEdgeConnected([makeQuery(id+"F25.opExtrude","SWEPT_FACE",FACE,{"disambiguationData":[OSD([sQuery(id+"F18.wireOp",EDGE,"E37.0")])]})])],"isStart":false});
            extrude(context, id + "F43", {"entities" : qUnion([Q0]), "operationType" : NewBodyOperationType.REMOVE, "endBound" : BoundingType.UP_TO_SURFACE, "depth" : 25 * mm, "endBoundEntityFace" : qUnion([Q1]), "hasOffset" : true, "offsetDistance" : 1 * mm, "hasDraft" : true, "draftAngle" : 1 * degree, "draftPullDirection" : true});
        }
        {
            var Q0;
            Q0=makeQuery(id+"F23.boolean.opBoolean","INTERSECT",EDGE,{"derivedFrom":[makeQuery(id+"F21.opExtrude","SWEPT_FACE",FACE,{"disambiguationData":[OSD([sQuery(id+"F20.wireOp",EDGE,"E39.0")])]}),makeQuery(id+"F23.opExtrude","SWEPT_FACE",FACE,{"disambiguationData":[OSD([sQuery(id+"F22.wireOp",EDGE,"E42")])]})]});
            fillet(context, id + "F44", {"entities" : qUnion([Q0]), "radius" : .5 * mm, "tangentPropagation" : true, "allowEdgeOverflow" : false});
        }
    });
